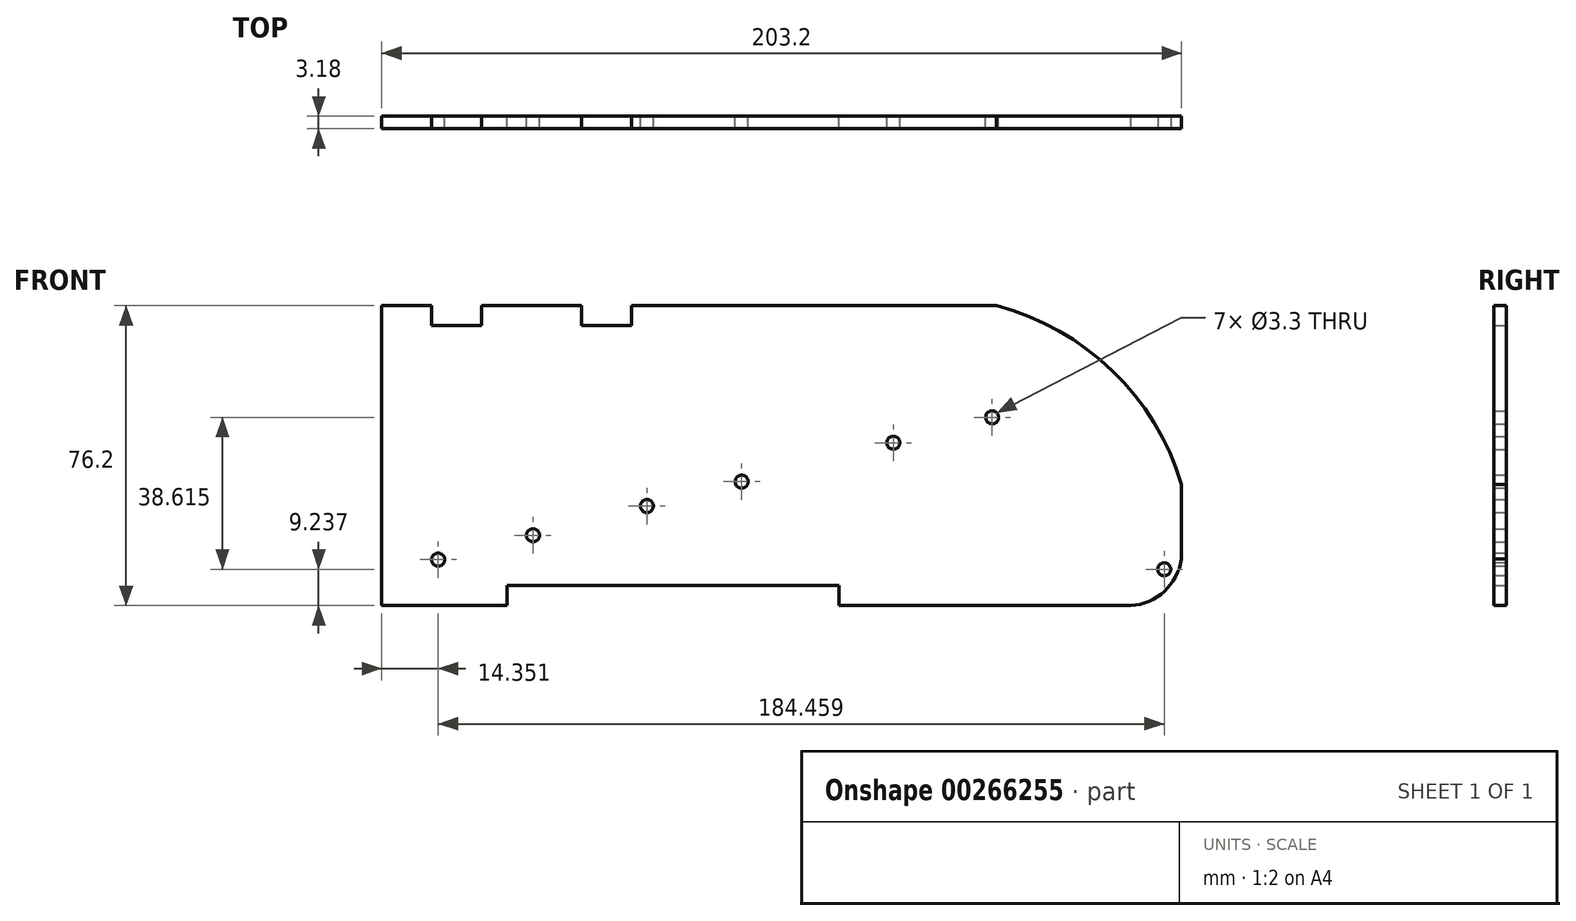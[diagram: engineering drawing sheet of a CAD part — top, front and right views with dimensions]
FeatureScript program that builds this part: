
annotation { "Feature Type Name" : "Feature", "Feature Type Description" : "" }
export const myFeature = defineFeature(function(context is Context, id is Id, definition is map)
    precondition{}
    {
        {
            var Q0;
            Q0=qCreatedBy(makeId("Front.planeOp"),FACE);
            var sketch = newSketch(context, id + "F0", { "sketchPlane" : qUnion([Q0])});
            skLineSegment(sketch, "E0.bottom", {"start": v(65.39, 0) * mm, "end": v(111.1, 0) * mm});
            skLineSegment(sketch, "E0.top", {"start": v(37.52, 76.2) * mm, "end": v(105.4, 76.2) * mm});
            skLineSegment(sketch, "E0.right", {"start": v(152.4, 11.85) * mm, "end": v(152.4, 30.8) * mm});
            skCircle(sketch, "E1", {"center": v(16.57, 25.32) * mm, "radius": 1.65 * mm});
            skCircle(sketch, "E2", {"center": v(40.65, 31.5) * mm, "radius": 1.65 * mm});
            skCircle(sketch, "E3", {"center": v(79.18, 41.4) * mm, "radius": 1.65 * mm});
            skCircle(sketch, "E4", {"center": v(104.3, 47.85) * mm, "radius": 1.65 * mm});
            skLineSegment(sketch, "E5", {"start": v(37.52, 76.2) * mm, "end": v(12.7, 76.2) * mm});
            skLineSegment(sketch, "E6", {"start": v(-50.8, 76.2) * mm, "end": v(-50.8, 0) * mm});
            skLineSegment(sketch, "E7", {"start": v(-50.8, 0) * mm, "end": v(-19.02, 0) * mm});
            skArc(sketch, "E8", {"start": v(152.4, 30.8) * mm, "mid": v(134.86, 59.67) * mm, "end": v(105.4, 76.2) * mm});
            skCircle(sketch, "E9", {"center": v(-12.36, 17.88) * mm, "radius": 1.65 * mm});
            skCircle(sketch, "E10", {"center": v(-36.45, 11.7) * mm, "radius": 1.65 * mm});
            skArc(sketch, "E11", {"start": v(139.48, 0) * mm, "mid": v(148, 3.66) * mm, "end": v(152.4, 11.85) * mm});
            skLineSegment(sketch, "E12.top", {"start": v(-19.02, 5.08) * mm, "end": v(65.39, 5.08) * mm});
            skLineSegment(sketch, "E12.left", {"start": v(-19.02, 0) * mm, "end": v(-19.02, 5.08) * mm});
            skLineSegment(sketch, "E12.right", {"start": v(65.39, 0) * mm, "end": v(65.39, 5.08) * mm});
            skLineSegment(sketch, "E13.trimOffspring", {"start": v(134.02, 0) * mm, "end": v(139.48, 0) * mm});
            skPoint(sketch, "E14.orphan", {"position": v(0, 0) * mm});
            skLineSegment(sketch, "E15.top", {"start": v(-38.1, 71.12) * mm, "end": v(-25.4, 71.12) * mm});
            skLineSegment(sketch, "E15.left", {"start": v(-38.1, 76.2) * mm, "end": v(-38.1, 71.12) * mm});
            skLineSegment(sketch, "E15.right", {"start": v(-25.4, 76.2) * mm, "end": v(-25.4, 71.12) * mm});
            skLineSegment(sketch, "E16.top", {"start": v(0, 71.12) * mm, "end": v(12.7, 71.12) * mm});
            skLineSegment(sketch, "E16.left", {"start": v(0, 76.2) * mm, "end": v(0, 71.12) * mm});
            skLineSegment(sketch, "E16.right", {"start": v(12.7, 76.2) * mm, "end": v(12.7, 71.12) * mm});
            skLineSegment(sketch, "E17.trimOffspring", {"start": v(-38.1, 76.2) * mm, "end": v(-50.8, 76.2) * mm});
            skLineSegment(sketch, "E18.trimOffspring", {"start": v(0, 76.2) * mm, "end": v(-25.4, 76.2) * mm});
            skLineSegment(sketch, "E19", {"start": v(134.02, 0) * mm, "end": v(139.05, 0) * mm});
            skLineSegment(sketch, "E20.top", {"start": v(111.1, 0) * mm, "end": v(139.05, 0) * mm});
            skLineSegment(sketch, "E20.left", {"start": v(111.1, 0) * mm, "end": v(111.1, 0) * mm});
            skLineSegment(sketch, "E20.right", {"start": v(139.05, 0) * mm, "end": v(139.05, 0) * mm});
            skSolve(sketch);
        }
        {
            var Q0;
            Q0 = qSketchRegion(id + "F0", true);
            extrude(context, id + "F1", {"entities" : qUnion([Q0]), "depth" : 3.17 * mm});
        }
        {
            var Q0;
            Q0=makeQuery(id+"F1.opExtrude","CAP_FACE",FACE,{"disambiguationData":[OSD([sQuery(id+"F0.wireOp",EDGE,"E0.bottom"),sQuery(id+"F0.wireOp",EDGE,"E0.top"),sQuery(id+"F0.wireOp",EDGE,"E0.right"),sQuery(id+"F0.wireOp",EDGE,"E1"),sQuery(id+"F0.wireOp",EDGE,"E2"),sQuery(id+"F0.wireOp",EDGE,"E3"),sQuery(id+"F0.wireOp",EDGE,"E4"),sQuery(id+"F0.wireOp",EDGE,"E5"),sQuery(id+"F0.wireOp",EDGE,"E6"),sQuery(id+"F0.wireOp",EDGE,"E7"),sQuery(id+"F0.wireOp",EDGE,"E8"),sQuery(id+"F0.wireOp",EDGE,"E9"),sQuery(id+"F0.wireOp",EDGE,"E10")])],"isStart":false});
            var sketch = newSketch(context, id + "F2", { "sketchPlane" : qUnion([Q0])});
            skCircle(sketch, "E21", {"center": v(148, 9.24) * mm, "radius": 1.65 * mm});
            skPoint(sketch, "E22", {"position": v(148, 3.66) * mm});
            skSolve(sketch);
        }
        {
            var Q0;
            Q0 = qSketchRegion(id + "F2", true);
            extrude(context, id + "F3", {"entities" : qUnion([Q0]), "operationType" : NewBodyOperationType.REMOVE, "oppositeDirection" : true, "depth" : 25.4 * mm});
        }
    });
